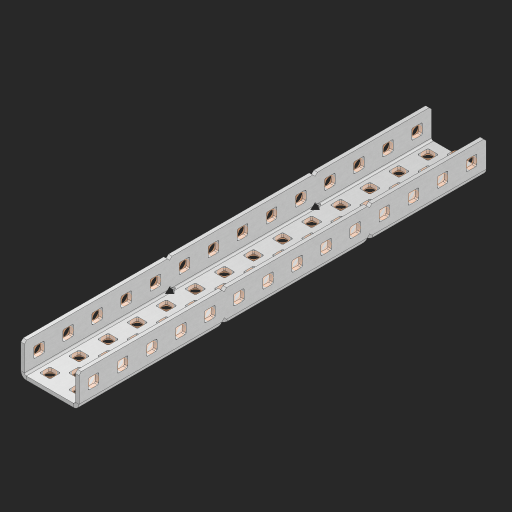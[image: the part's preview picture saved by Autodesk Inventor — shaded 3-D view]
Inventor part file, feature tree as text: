
AUTODESK INVENTOR PART (.ipt)
format: ipt  version: 2023 (Build 270158000, 158)  size: 1,120,768 bytes
history: native  units: in
note: dims shown in document units (in); Inventor stores cm internally (conversion verified against a paired STEP export)
features: other x77, extrude x68, sheet_metal_op x11, sketch x10, pattern_linear x2, mirror x1, chamfer x1
ambient origin geometry x8: Origin, YZ Plane, XZ Plane, XY Plane, X Axis, Y Axis, Z Axis, Center Point
bodies: Solid1 (feature_tree), Body (feature_tree)
feature tree (170):
  sheet_metal_op  "Flanges"
  other  "Flange Pattern Plane"
  other  "Flange Pattern Sketch"
  sheet_metal_op  "Flange Pattern"
  sheet_metal_op  "Body Pattern"
  pattern_linear  "Center Pattern"  Spacing1=0.0625in  [1 undecoded]
  other  "Arc Length"
  mirror  "Notch Mirror"
  pattern_linear  "Notch Pattern"  Spacing1=0.182in  [1 undecoded]
  chamfer  "End Chamfer"
  extrude  "Half Cut"  Depth=0.02in
  sketch  "Sketch1"  dims[d0=1.0in]
  other  "Plate1"
  sketch  "Sketch2"  dims[d1=7.0in]
  other  "Plate2"
  sheet_metal_op  "Bend1"
  sheet_metal_op  "Corner1"
  sketch  "Sketch3"  dims[d2=0.0625in]
  sketch  "Sketch7"  dims[d3=0.0625in]
  other  "Srf1"
  other  "Srf2"
  sketch  "Sketch8"  dims[d4=0.0312in]
  sketch  "Sketch9"  dims[d5=0.125in]
  other  "Srf91"
  sheet_metal_op  "Body Pattern Sketch"
  other  "Srf92"
  sketch  "Sketch13"  dims[d6=0.0625in]
  sketch  "Sketch14"  dims[d7=0.5in d8=90.0deg d9=0.0312in]
  sketch  "Sketch15"  dims[d10=0.25in]
  sketch  "Sketch16"  dims[d11=0.0625in d12=0.0625in d16=0.182in d17=0.02in d18=0.0625in d19=0.0in d20=0.25in d21=0.25in d38=5.5118in d40=0.5in d41=0.7874in d43=1.0in d46=0.172in d47=1.0in d48=0.0in d49=0.182in d50=0.02in d51=0.25in d52=0.25in d53=0.0625in d54=0.0in d55=0.172in d56=1.0in d57=0.0in d58=0.25in d60=5.5118in d62=0.5in d63=0.7874in d65=0.5in d85=0.1473in d86=0.1782in d88=0.04in d89=0.0625in d90=0.0in d91=0.04in d92=0.0491in d95=2.5in d96=0.04in d97=0.25in d98=45.0deg d99=0.25in d100=0.5in d101=0.0in d102=2.497in d106=0.182in d107=0.02in d108=0.5in d109=0.5in d110=0.0625in d111=0.0in d112=0.172in d113=0.5in d114=0.0in d117=0.5in d118=0.5in d119=0.5in]
  other  "Srf786"
  other  "Srf823"
  other  "Srf824"
  other  "Srf825"
  other  "Srf826"
  other  "Srf827"
  other  "Srf828"
  other  "Srf829"
  other  "Srf856"
  other  "Srf857"
  other  "Srf858"
  other  "Srf859"
  other  "Srf860"
  other  "Srf861"
  other  "Srf862"
  other  "Srf889"
  other  "Srf890"
  other  "Srf891"
  other  "Srf892"
  other  "Srf893"
  other  "Srf894"
  other  "Srf895"
  other  "Srf896"
  other  "Srf922"
  other  "Srf923"
  other  "Srf924"
  other  "Srf925"
  other  "Srf926"
  other  "Srf959"
  other  "Srf960"
  other  "Srf961"
  other  "Srf962"
  other  "Srf963"
  other  "Srf996"
  other  "Srf997"
  other  "Srf998"
  other  "Srf999"
  other  "Srf1000"
  other  "Srf1143"
  other  "Srf1144"
  other  "Srf1145"
  other  "Srf1146"
  other  "Srf1147"
  other  "Srf1148"
  other  "Srf1149"
  other  "Srf1150"
  other  "Srf1151"
  other  "Srf1152"
  other  "Srf1153"
  other  "Srf1154"
  other  "Srf1155"
  other  "Srf1156"
  other  "Srf1199"
  other  "Srf1200"
  other  "Srf1201"
  other  "Srf1202"
  other  "Srf1203"
  other  "Srf1204"
  other  "Srf1205"
  other  "Srf1206"
  other  "Srf1207"
  other  "Srf1208"
  other  "Srf1209"
  other  "Srf1210"
  other  "Srf1211"
  other  "Srf1212"
  sheet_metal_op  "Flange Stamp"
  sheet_metal_op  "Flange Circle"
  sheet_metal_op  "Body Stamp"
  sheet_metal_op  "Body Circle"
  other  "Center Stamp"
  other  "Center Circle"
  sheet_metal_op  "Notch"
  extrude  "ExtrusionSrf2"  Depth=0.0625in
  extrude  "ExtrusionSrf92"  TaperAngle=0.0deg  [1 undecoded]
  extrude  "ExtrusionSrf823"  Depth=0.5in
  extrude  "ExtrusionSrf824"  Depth=0.5in
  extrude  "ExtrusionSrf825"  Depth=0.5in
  extrude  "ExtrusionSrf826"  Depth=0.5in
  extrude  "ExtrusionSrf827"  Depth=1.0in TaperAngle=0.0deg
  extrude  "ExtrusionSrf828"  Depth=0.5in
  extrude  "ExtrusionSrf829"  Depth=0.02in
  extrude  "ExtrusionSrf856"  Depth=0.5in
  extrude  "ExtrusionSrf857"  Depth=0.5in
  extrude  "ExtrusionSrf858"  Depth=0.0625in
  extrude  "ExtrusionSrf859"  TaperAngle=0.0deg  [1 undecoded]
  extrude  "ExtrusionSrf860"  Depth=0.5in
  extrude  "ExtrusionSrf861"  Depth=1.0in TaperAngle=0.0deg
  extrude  "ExtrusionSrf862"  Depth=0.5in
  extrude  "ExtrusionSrf889"  Depth=0.5in
  extrude  "ExtrusionSrf890"  Depth=0.5in
  extrude  "ExtrusionSrf891"  Depth=0.5in
  extrude  "ExtrusionSrf892"  Depth=0.5in
  extrude  "ExtrusionSrf893"  Depth=0.5in
  extrude  "ExtrusionSrf894"  Depth=0.0625in
  extrude  "ExtrusionSrf895"  TaperAngle=0.0deg  [1 undecoded]
  extrude  "ExtrusionSrf896"  Depth=0.5in
  extrude  "ExtrusionSrf922"  Depth=0.5in
  extrude  "ExtrusionSrf923"  Depth=2.5in
  extrude  "ExtrusionSrf924"  Depth=0.5in TaperAngle=45.0deg
  extrude  "ExtrusionSrf925"  Depth=0.5in
  extrude  "ExtrusionSrf926"  Depth=0.5in TaperAngle=0.0deg
  extrude  "ExtrusionSrf959"  Depth=0.5in
  extrude  "ExtrusionSrf960"  Depth=0.5in
  extrude  "ExtrusionSrf961"  Depth=0.02in
  extrude  "ExtrusionSrf962"  Depth=0.5in
  extrude  "ExtrusionSrf963"  Depth=0.5in
  extrude  "ExtrusionSrf996"  Depth=0.0625in
  extrude  "ExtrusionSrf997"  TaperAngle=0.0deg  [1 undecoded]
  extrude  "ExtrusionSrf998"  Depth=0.5in
  extrude  "ExtrusionSrf999"  Depth=0.5in TaperAngle=0.0deg
  extrude  "ExtrusionSrf1000"  Depth=0.5in
  extrude  "ExtrusionSrf1143"  Depth=0.5in
  extrude  "ExtrusionSrf1144"  Depth=0.5in
  extrude  "ExtrusionSrf1145"  [1 undecoded]
  extrude  "ExtrusionSrf1146"  [1 undecoded]
  extrude  "ExtrusionSrf1147"  [1 undecoded]
  extrude  "ExtrusionSrf1148"  [1 undecoded]
  extrude  "ExtrusionSrf1149"  [1 undecoded]
  extrude  "ExtrusionSrf1150"  [1 undecoded]
  extrude  "ExtrusionSrf1151"  [1 undecoded]
  extrude  "ExtrusionSrf1152"  [1 undecoded]
  extrude  "ExtrusionSrf1153"  [1 undecoded]
  extrude  "ExtrusionSrf1154"  [1 undecoded]
  extrude  "ExtrusionSrf1155"  [1 undecoded]
  extrude  "ExtrusionSrf1156"  [1 undecoded]
  extrude  "ExtrusionSrf1199"  [1 undecoded]
  extrude  "ExtrusionSrf1200"  [1 undecoded]
  extrude  "ExtrusionSrf1201"  [1 undecoded]
  extrude  "ExtrusionSrf1202"  [1 undecoded]
  extrude  "ExtrusionSrf1203"  [1 undecoded]
  extrude  "ExtrusionSrf1204"  [1 undecoded]
  extrude  "ExtrusionSrf1205"  [1 undecoded]
  extrude  "ExtrusionSrf1206"  [1 undecoded]
  extrude  "ExtrusionSrf1207"  [1 undecoded]
  extrude  "ExtrusionSrf1208"  [1 undecoded]
  extrude  "ExtrusionSrf1209"  [1 undecoded]
  extrude  "ExtrusionSrf1210"  [1 undecoded]
  extrude  "ExtrusionSrf1211"  [1 undecoded]
  extrude  "ExtrusionSrf1212"  [1 undecoded]
note: 32 required parameter values undecoded (feature->parameter linkage not recoverable at this tier; creation-order binding heuristic only, values carry confidence <= 0.55)
